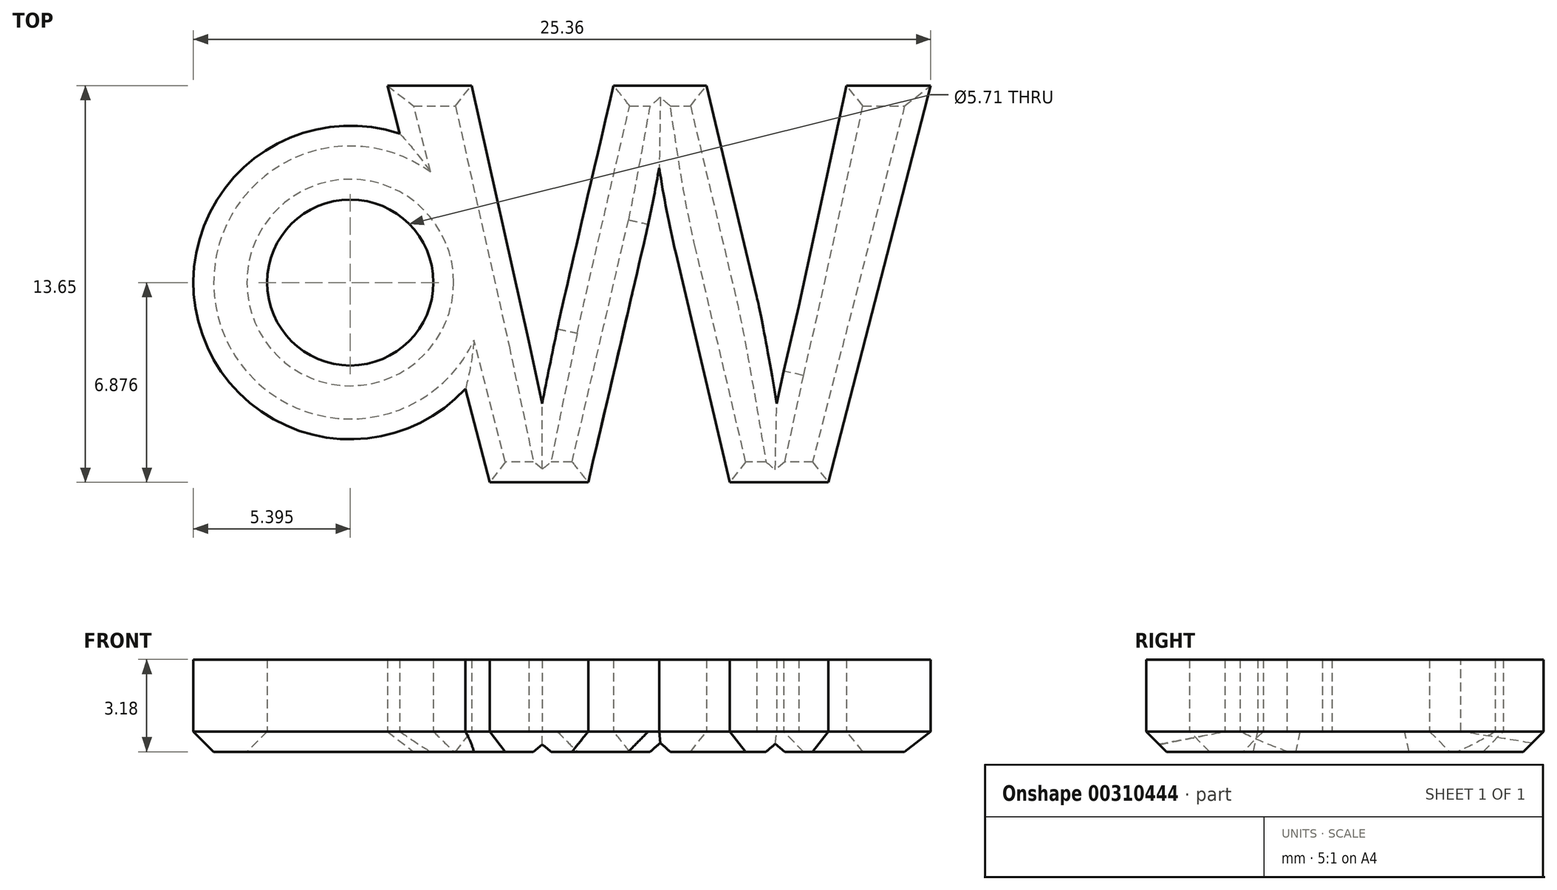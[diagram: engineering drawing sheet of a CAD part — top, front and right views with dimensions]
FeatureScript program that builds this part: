
annotation { "Feature Type Name" : "Feature", "Feature Type Description" : "" }
export const myFeature = defineFeature(function(context is Context, id is Id, definition is map)
    precondition{}
    {
        {
            var Q0;
            Q0=qCreatedBy(makeId("Top.planeOp"),FACE);
            var sketch = newSketch(context, id + "F0", { "sketchPlane" : qUnion([Q0])});
            skText(sketch, "E0", { "text": "W", "fontName": "Arimo-Bold.ttf"});
            skCircle(sketch, "E1", {"center": v(-1.25, -7.41) * mm, "radius": 5.4 * mm});
            skCircle(sketch, "E2", {"center": v(-1.25, -7.41) * mm, "radius": 2.86 * mm});
            const initialGuessF0  = {"E0": [0, -0.01429, 1, 0, 0.01429]};
            skSetInitialGuess(sketch, initialGuessF0);
            skSolve(sketch);
        }
        {
            var Q0;
            Q0=qSketchRegion(id+"F0",true);
            var Q1;
            Q1=qSketchRegion(id+"FFuAMvX4B0CXexs_0",true);
            var Q2;
            Q2=qSketchRegion(id+"F3e2CQsKu9PIjX0_0",true);
            var Q3;
            Q3=qSketchRegion(id+"F9LWrLlmn86MAX7_0",true);
            extrude(context, id + "F1", {"entities" : qUnion([Q0, Q1, Q2, Q3]), "depth" : 3.17 * mm});
        }
        {
            var Q0;
            Q0=makeQuery(id+"F1.opExtrude","CAP_FACE",FACE,{"disambiguationData":[OSD([sQuery(id+"F3e2CQsKu9PIjX0_0.wireOp",EDGE,"d36403c4-1396-490d-9497-49aafdbeb43d.sketch_text.stroke-0"),sQuery(id+"F3e2CQsKu9PIjX0_0.wireOp",EDGE,"d36403c4-1396-490d-9497-49aafdbeb43d.sketch_text.stroke-1"),sQuery(id+"F3e2CQsKu9PIjX0_0.wireOp",EDGE,"d36403c4-1396-490d-9497-49aafdbeb43d.sketch_text.stroke-2"),sQuery(id+"F3e2CQsKu9PIjX0_0.wireOp",EDGE,"d36403c4-1396-490d-9497-49aafdbeb43d.sketch_text.stroke-3"),sQuery(id+"F3e2CQsKu9PIjX0_0.wireOp",EDGE,"d36403c4-1396-490d-9497-49aafdbeb43d.sketch_text.stroke-4"),sQuery(id+"F3e2CQsKu9PIjX0_0.wireOp",EDGE,"d36403c4-1396-490d-9497-49aafdbeb43d.sketch_text.stroke-5"),sQuery(id+"F3e2CQsKu9PIjX0_0.wireOp",EDGE,"d36403c4-1396-490d-9497-49aafdbeb43d.sketch_text.stroke-6"),sQuery(id+"F3e2CQsKu9PIjX0_0.wireOp",EDGE,"d36403c4-1396-490d-9497-49aafdbeb43d.sketch_text.stroke-7"),sQuery(id+"F3e2CQsKu9PIjX0_0.wireOp",EDGE,"d36403c4-1396-490d-9497-49aafdbeb43d.sketch_text.stroke-8"),sQuery(id+"F3e2CQsKu9PIjX0_0.wireOp",EDGE,"d36403c4-1396-490d-9497-49aafdbeb43d.sketch_text.stroke-9"),sQuery(id+"F3e2CQsKu9PIjX0_0.wireOp",EDGE,"d36403c4-1396-490d-9497-49aafdbeb43d.sketch_text.stroke-10"),sQuery(id+"F3e2CQsKu9PIjX0_0.wireOp",EDGE,"d36403c4-1396-490d-9497-49aafdbeb43d.sketch_text.stroke-11"),sQuery(id+"F3e2CQsKu9PIjX0_0.wireOp",EDGE,"d36403c4-1396-490d-9497-49aafdbeb43d.sketch_text.stroke-12"),sQuery(id+"F3e2CQsKu9PIjX0_0.wireOp",EDGE,"d36403c4-1396-490d-9497-49aafdbeb43d.sketch_text.stroke-13"),sQuery(id+"F3e2CQsKu9PIjX0_0.wireOp",EDGE,"d36403c4-1396-490d-9497-49aafdbeb43d.sketch_text.stroke-14"),sQuery(id+"F3e2CQsKu9PIjX0_0.wireOp",EDGE,"d36403c4-1396-490d-9497-49aafdbeb43d.sketch_text.stroke-15"),sQuery(id+"F3e2CQsKu9PIjX0_0.wireOp",EDGE,"d36403c4-1396-490d-9497-49aafdbeb43d.sketch_text.stroke-16"),sQuery(id+"F3e2CQsKu9PIjX0_0.wireOp",EDGE,"d36403c4-1396-490d-9497-49aafdbeb43d.sketch_text.stroke-17"),sQuery(id+"F3e2CQsKu9PIjX0_0.wireOp",EDGE,"d36403c4-1396-490d-9497-49aafdbeb43d.sketch_text.stroke-18"),sQuery(id+"F3e2CQsKu9PIjX0_0.wireOp",EDGE,"d36403c4-1396-490d-9497-49aafdbeb43d.sketch_text.stroke-19"),sQuery(id+"F3e2CQsKu9PIjX0_0.wireOp",EDGE,"d36403c4-1396-490d-9497-49aafdbeb43d.sketch_text.stroke-20")])],"isStart":true});
            var Q1;
            Q1=makeQuery(id+"F1.opExtrude","CAP_FACE",FACE,{"disambiguationData":[OSD([sQuery(id+"FFuAMvX4B0CXexs_0.wireOp",EDGE,"ff5d8e69-f4ea-49cc-82ca-cbd897854416.sketch_text.stroke-0"),sQuery(id+"FFuAMvX4B0CXexs_0.wireOp",EDGE,"ff5d8e69-f4ea-49cc-82ca-cbd897854416.sketch_text.stroke-1"),sQuery(id+"FFuAMvX4B0CXexs_0.wireOp",EDGE,"ff5d8e69-f4ea-49cc-82ca-cbd897854416.sketch_text.stroke-2"),sQuery(id+"FFuAMvX4B0CXexs_0.wireOp",EDGE,"ff5d8e69-f4ea-49cc-82ca-cbd897854416.sketch_text.stroke-3"),sQuery(id+"FFuAMvX4B0CXexs_0.wireOp",EDGE,"ff5d8e69-f4ea-49cc-82ca-cbd897854416.sketch_text.stroke-4"),sQuery(id+"FFuAMvX4B0CXexs_0.wireOp",EDGE,"ff5d8e69-f4ea-49cc-82ca-cbd897854416.sketch_text.stroke-5"),sQuery(id+"FFuAMvX4B0CXexs_0.wireOp",EDGE,"ff5d8e69-f4ea-49cc-82ca-cbd897854416.sketch_text.stroke-6"),sQuery(id+"FFuAMvX4B0CXexs_0.wireOp",EDGE,"ff5d8e69-f4ea-49cc-82ca-cbd897854416.sketch_text.stroke-7"),sQuery(id+"FFuAMvX4B0CXexs_0.wireOp",EDGE,"ff5d8e69-f4ea-49cc-82ca-cbd897854416.sketch_text.stroke-8"),sQuery(id+"FFuAMvX4B0CXexs_0.wireOp",EDGE,"ff5d8e69-f4ea-49cc-82ca-cbd897854416.sketch_text.stroke-9"),sQuery(id+"FFuAMvX4B0CXexs_0.wireOp",EDGE,"ff5d8e69-f4ea-49cc-82ca-cbd897854416.sketch_text.stroke-10"),sQuery(id+"FFuAMvX4B0CXexs_0.wireOp",EDGE,"ff5d8e69-f4ea-49cc-82ca-cbd897854416.sketch_text.stroke-11"),sQuery(id+"FFuAMvX4B0CXexs_0.wireOp",EDGE,"ff5d8e69-f4ea-49cc-82ca-cbd897854416.sketch_text.stroke-12"),sQuery(id+"FFuAMvX4B0CXexs_0.wireOp",EDGE,"ff5d8e69-f4ea-49cc-82ca-cbd897854416.sketch_text.stroke-13"),sQuery(id+"FFuAMvX4B0CXexs_0.wireOp",EDGE,"ff5d8e69-f4ea-49cc-82ca-cbd897854416.sketch_text.stroke-14"),sQuery(id+"FFuAMvX4B0CXexs_0.wireOp",EDGE,"ff5d8e69-f4ea-49cc-82ca-cbd897854416.sketch_text.stroke-15"),sQuery(id+"FFuAMvX4B0CXexs_0.wireOp",EDGE,"ff5d8e69-f4ea-49cc-82ca-cbd897854416.sketch_text.stroke-16")])],"isStart":true});
            var Q2;
            Q2=makeQuery(id+"F1.opExtrude","CAP_FACE",FACE,{"disambiguationData":[OSD([sQuery(id+"F9LWrLlmn86MAX7_0.wireOp",EDGE,"c90eff37-dab6-43ec-bed2-d4ad99606f9c.sketch_text.stroke-0"),sQuery(id+"F9LWrLlmn86MAX7_0.wireOp",EDGE,"c90eff37-dab6-43ec-bed2-d4ad99606f9c.sketch_text.stroke-1"),sQuery(id+"F9LWrLlmn86MAX7_0.wireOp",EDGE,"c90eff37-dab6-43ec-bed2-d4ad99606f9c.sketch_text.stroke-2"),sQuery(id+"F9LWrLlmn86MAX7_0.wireOp",EDGE,"c90eff37-dab6-43ec-bed2-d4ad99606f9c.sketch_text.stroke-3"),sQuery(id+"F9LWrLlmn86MAX7_0.wireOp",EDGE,"c90eff37-dab6-43ec-bed2-d4ad99606f9c.sketch_text.stroke-4"),sQuery(id+"F9LWrLlmn86MAX7_0.wireOp",EDGE,"c90eff37-dab6-43ec-bed2-d4ad99606f9c.sketch_text.stroke-5"),sQuery(id+"F9LWrLlmn86MAX7_0.wireOp",EDGE,"c90eff37-dab6-43ec-bed2-d4ad99606f9c.sketch_text.stroke-6"),sQuery(id+"F9LWrLlmn86MAX7_0.wireOp",EDGE,"c90eff37-dab6-43ec-bed2-d4ad99606f9c.sketch_text.stroke-7"),sQuery(id+"F9LWrLlmn86MAX7_0.wireOp",EDGE,"c90eff37-dab6-43ec-bed2-d4ad99606f9c.sketch_text.stroke-8"),sQuery(id+"F9LWrLlmn86MAX7_0.wireOp",EDGE,"c90eff37-dab6-43ec-bed2-d4ad99606f9c.sketch_text.stroke-9"),sQuery(id+"F9LWrLlmn86MAX7_0.wireOp",EDGE,"c90eff37-dab6-43ec-bed2-d4ad99606f9c.sketch_text.stroke-10"),sQuery(id+"F9LWrLlmn86MAX7_0.wireOp",EDGE,"c90eff37-dab6-43ec-bed2-d4ad99606f9c.sketch_text.stroke-11"),sQuery(id+"F9LWrLlmn86MAX7_0.wireOp",EDGE,"c90eff37-dab6-43ec-bed2-d4ad99606f9c.sketch_text.stroke-12"),sQuery(id+"F9LWrLlmn86MAX7_0.wireOp",EDGE,"c90eff37-dab6-43ec-bed2-d4ad99606f9c.sketch_text.stroke-13"),sQuery(id+"F9LWrLlmn86MAX7_0.wireOp",EDGE,"c90eff37-dab6-43ec-bed2-d4ad99606f9c.sketch_text.stroke-14"),sQuery(id+"F9LWrLlmn86MAX7_0.wireOp",EDGE,"c90eff37-dab6-43ec-bed2-d4ad99606f9c.sketch_text.stroke-15"),sQuery(id+"F9LWrLlmn86MAX7_0.wireOp",EDGE,"c90eff37-dab6-43ec-bed2-d4ad99606f9c.sketch_text.stroke-16")])],"isStart":true});
            var Q3;
            Q3=makeQuery(id+"F1.opExtrude","CAP_FACE",FACE,{"disambiguationData":[OSD([sQuery(id+"F0.wireOp",EDGE,"E0.sketch_text.stroke-0"),sQuery(id+"F0.wireOp",EDGE,"E0.sketch_text.stroke-1"),sQuery(id+"F0.wireOp",EDGE,"E0.sketch_text.stroke-2"),sQuery(id+"F0.wireOp",EDGE,"E0.sketch_text.stroke-3"),sQuery(id+"F0.wireOp",EDGE,"E0.sketch_text.stroke-4"),sQuery(id+"F0.wireOp",EDGE,"E0.sketch_text.stroke-5"),sQuery(id+"F0.wireOp",EDGE,"E0.sketch_text.stroke-6"),sQuery(id+"F0.wireOp",EDGE,"E0.sketch_text.stroke-7"),sQuery(id+"F0.wireOp",EDGE,"E0.sketch_text.stroke-8"),sQuery(id+"F0.wireOp",EDGE,"E0.sketch_text.stroke-9"),sQuery(id+"F0.wireOp",EDGE,"E0.sketch_text.stroke-10"),sQuery(id+"F0.wireOp",EDGE,"E0.sketch_text.stroke-11"),sQuery(id+"F0.wireOp",EDGE,"E0.sketch_text.stroke-12"),sQuery(id+"F0.wireOp",EDGE,"E0.sketch_text.stroke-13"),sQuery(id+"F0.wireOp",EDGE,"E0.sketch_text.stroke-14"),sQuery(id+"F0.wireOp",EDGE,"E0.sketch_text.stroke-15"),sQuery(id+"F0.wireOp",EDGE,"E0.sketch_text.stroke-16"),sQuery(id+"F0.wireOp",EDGE,"E0.sketch_text.stroke-17"),sQuery(id+"F0.wireOp",EDGE,"E0.sketch_text.stroke-18"),sQuery(id+"F0.wireOp",EDGE,"E0.sketch_text.stroke-19"),sQuery(id+"F0.wireOp",EDGE,"E1"),sQuery(id+"F0.wireOp",EDGE,"E2")])],"isStart":true});
            chamfer(context, id + "F2", {"entities" : qUnion([Q0, Q1, Q2, Q3]), "width" : 0.7 * mm, "tangentPropagation" : true});
        }
    });
